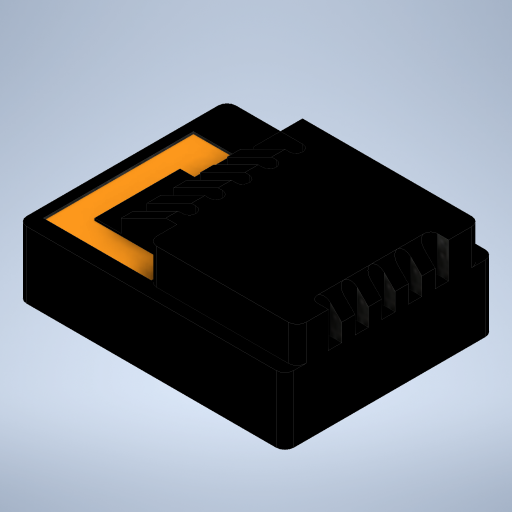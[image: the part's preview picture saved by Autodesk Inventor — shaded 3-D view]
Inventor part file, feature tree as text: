
AUTODESK INVENTOR PART (.ipt)
format: ipt  version: 2023 (Build 270158000, 158)  size: 397,824 bytes
history: native  units: in
note: dims shown in document units (in); Inventor stores cm internally (conversion verified against a paired STEP export)
features: extrude x9, sketch x8, fillet x2
ambient origin geometry x8: Origin, YZ Plane, XZ Plane, XY Plane, X Axis, Y Axis, Z Axis, Center Point
bodies: Solid1 (feature_tree)
feature tree (19):
  extrude  "Extrusion1"  Depth=2.3622in
  fillet  "Fillet1"  Radius=0.5906in
  extrude  "Extrusion2"  Depth=1.3189in
  fillet  "Fillet2"  Radius=1.622in
  extrude  "Extrusion3"  Depth=0.2559in
  extrude  "Extrusion4"  Depth=0.315in TaperAngle=0.0deg
  extrude  "Extrusion5"  Depth=0.3937in
  extrude  "Extrusion6"  Depth=1.063in TaperAngle=0.0deg
  sketch  "Sketch7"  dims[d17=0.2362in d18=0.2362in]
  extrude  "Extrusion7"  Depth=0.2362in
  extrude  "Extrusion8"  Depth=0.1181in
  extrude  "Extrusion9"  Depth=0.0591in
  sketch  "Sketch1"  dims[d0=1.8504in d1=2.3622in d2=0.5906in d3=0.0in]
  sketch  "Sketch2"  dims[d4=0.0787in d5=1.3189in d6=1.622in]
  sketch  "Sketch3"  dims[d7=0.1083in d8=0.2559in]
  sketch  "Sketch4"  dims[d9=1.811in d10=0.315in d11=0.0in]
  sketch  "Sketch5"  dims[d12=0.0787in d13=0.3937in]
  sketch  "Sketch6"  dims[d14=0.1181in d15=1.063in d16=0.0in]
  sketch  "Sketch9"  dims[d19=0.1969in d20=0.0in d21=0.1181in d22=0.0591in d23=0.1083in d24=0.4331in d25=1.9685in d27=0.2362in d28=0.3937in d30=0.3937in d32=0.315in d33=0.0in d35=0.0591in d36=0.1181in d37=0.0984in d38=0.2756in d39=1.9685in d41=0.2362in d42=0.3937in d44=0.3937in d46=0.315in d47=0.0in d52=0.1575in d53=0.1575in d54=0.8858in d55=0.0in d56=0.0591in d57=0.0in d58=0.3543in d59=0.2264in d60=0.9547in d61=1.3268in d62=0.3445in d63=0.0886in d64=0.1378in d65=0.2264in d66=0.0197in d67=0.0in]
